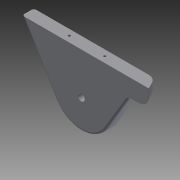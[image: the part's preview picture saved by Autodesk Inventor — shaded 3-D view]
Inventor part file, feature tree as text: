
AUTODESK INVENTOR PART (.ipt)
format: ipt  version: 2015 (Build 190159000, 159)  size: 198,656 bytes
history: native  units: mm
features: extrude x5, sketch x5, fillet x4
ambient origin geometry x8: Origin, YZ Plane, XZ Plane, XY Plane, X Axis, Y Axis, Z Axis, Center Point
bodies: Solid1 (feature_tree)
feature tree (14):
  extrude  "Extrusion1"  Depth=50.0mm
  extrude  "Extrusion2"  Depth=6.0mm
  extrude  "Extrusion3"  Depth=2.0mm
  extrude  "Extrusion4"  Depth=10.0mm TaperAngle=0.0deg
  extrude  "Extrusion5"  Depth=10.0mm
  fillet  "Fillet1"  Radius=10.0mm
  fillet  "Fillet2"  Radius=6.4mm
  fillet  "Fillet3"  Radius=48.5mm
  fillet  "Fillet4"  [1 undecoded]
  sketch  "Sketch1"  dims[d4=50.0mm d5=50.0mm]
  sketch  "Sketch2"  dims[d6=100.0mm d7=6.0mm]
  sketch  "Sketch3"  dims[d8=10.0mm d9=0.0mm d11=2.0mm]
  sketch  "Sketch4"  dims[d12=2.0mm d13=10.0mm d14=0.0mm]
  sketch  "Sketch5"  dims[d15=15.0mm d16=10.0mm d17=10.0mm d18=0.0mm d19=6.4mm d20=0.0mm d21=48.5mm d22=90.0deg d23=124.0mm d24=15.0mm d25=0.0mm d26=8.0mm d27=8.0mm d28=2.0mm d29=0.2mm]
note: 1 required parameter value undecoded (feature->parameter linkage not recoverable at this tier; creation-order binding heuristic only, values carry confidence <= 0.55)
